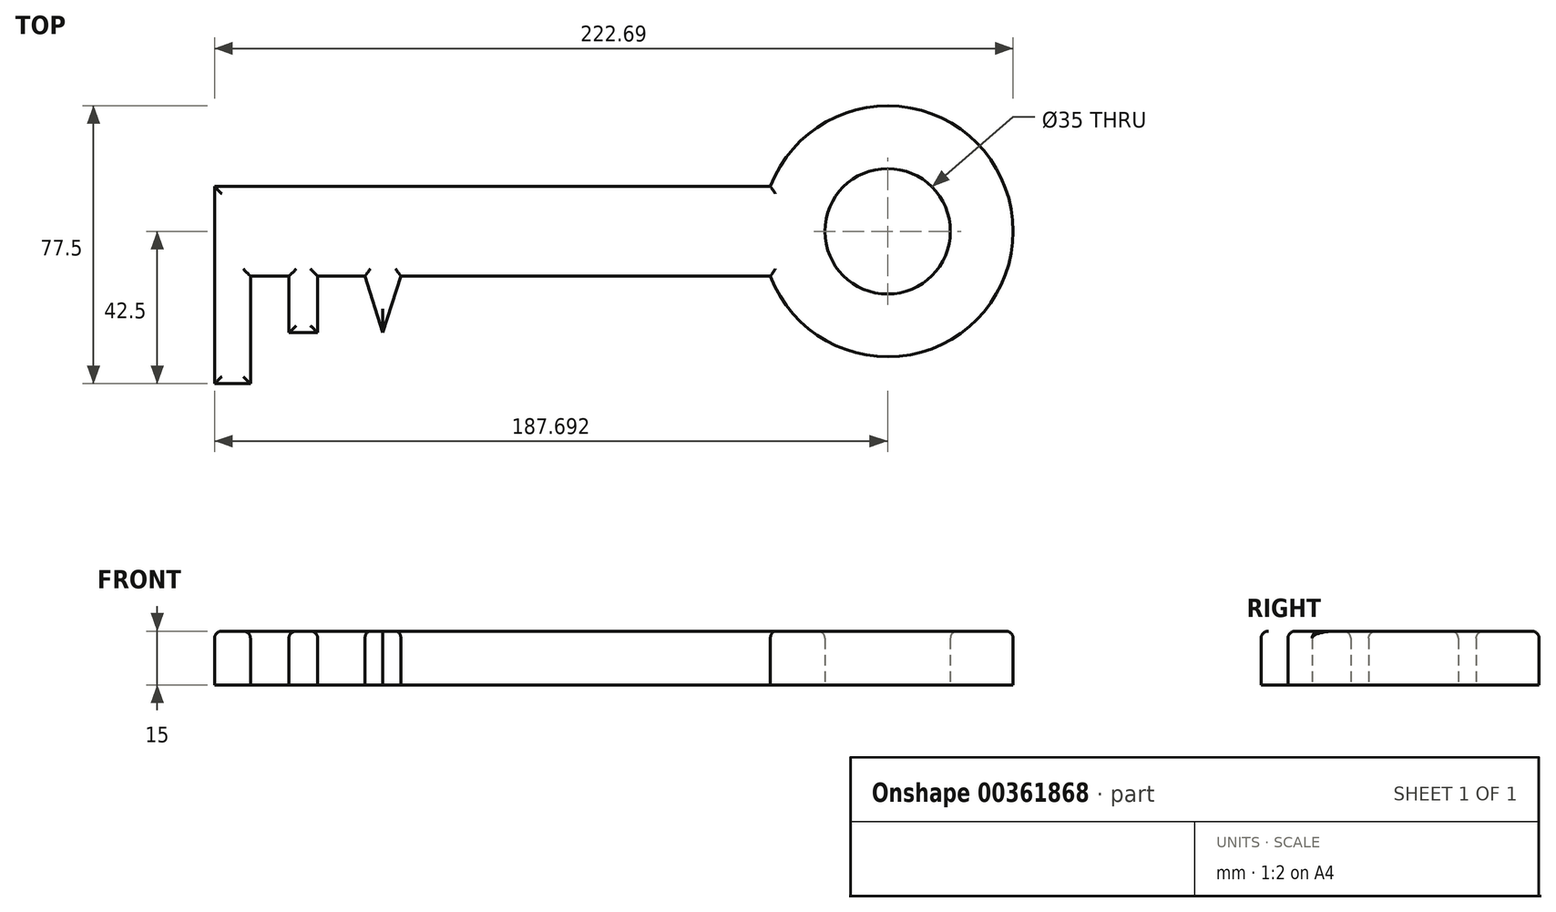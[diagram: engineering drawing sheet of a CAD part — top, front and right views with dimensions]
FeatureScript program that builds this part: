
annotation { "Feature Type Name" : "Feature", "Feature Type Description" : "" }
export const myFeature = defineFeature(function(context is Context, id is Id, definition is map)
    precondition{}
    {
        {
            var Q0;
            Q0=qCreatedBy(makeId("Top.planeOp"),FACE);
            var sketch = newSketch(context, id + "F0", { "sketchPlane" : qUnion([Q0])});
            skLineSegment(sketch, "E0.bottom", {"start": v(0, 15.78) * mm, "end": v(-155, 15.78) * mm});
            skLineSegment(sketch, "E0.top", {"start": v(0, 40.78) * mm, "end": v(-155, 40.78) * mm});
            skLineSegment(sketch, "E0.right", {"start": v(-155, 15.78) * mm, "end": v(-155, 40.78) * mm});
            skLineSegment(sketch, "E1.bottom", {"start": v(-155, 15.78) * mm, "end": v(-145, 15.78) * mm});
            skLineSegment(sketch, "E1.top", {"start": v(-155, -14.22) * mm, "end": v(-145, -14.22) * mm});
            skLineSegment(sketch, "E1.left", {"start": v(-155, 15.78) * mm, "end": v(-155, -14.22) * mm});
            skLineSegment(sketch, "E1.right", {"start": v(-145, 15.78) * mm, "end": v(-145, -14.22) * mm});
            skLineSegment(sketch, "E2.bottom", {"start": v(-134.26, 15.78) * mm, "end": v(-126.26, 15.78) * mm});
            skLineSegment(sketch, "E2.top", {"start": v(-134.26, 0) * mm, "end": v(-126.26, 0) * mm});
            skLineSegment(sketch, "E2.left", {"start": v(-134.26, 15.78) * mm, "end": v(-134.26, 0) * mm});
            skLineSegment(sketch, "E2.right", {"start": v(-126.26, 15.78) * mm, "end": v(-126.26, 0) * mm});
            skLineSegment(sketch, "E3", {"start": v(-113.05, 15.78) * mm, "end": v(-103.05, 15.78) * mm});
            skLineSegment(sketch, "E4", {"start": v(-113.05, 15.78) * mm, "end": v(-108.05, 0) * mm});
            skLineSegment(sketch, "E5", {"start": v(-108.05, 0) * mm, "end": v(-103.05, 15.78) * mm});
            skArc(sketch, "E6", {"start": v(0, 15.78) * mm, "mid": v(67.7, 28.28) * mm, "end": v(0, 40.78) * mm});
            skCircle(sketch, "E7", {"center": v(32.7, 28.28) * mm, "radius": 17.5 * mm});
            skSolve(sketch);
        }
        {
            var Q0;
            Q0 = qSketchRegion(id + "F0", true);
            extrude(context, id + "F1", {"entities" : qUnion([Q0]), "depth" : 15 * mm});
        }
        {
            var Q0;
            Q0=makeQuery(id+"F1.opExtrude","CAP_FACE",FACE,{"disambiguationData":[OSD([sQuery(id+"F0.wireOp",EDGE,"E0.bottom"),sQuery(id+"F0.wireOp",EDGE,"E0.top"),sQuery(id+"F0.wireOp",EDGE,"E0.right"),sQuery(id+"F0.wireOp",EDGE,"E1.top"),sQuery(id+"F0.wireOp",EDGE,"E1.left"),sQuery(id+"F0.wireOp",EDGE,"E1.right"),sQuery(id+"F0.wireOp",EDGE,"E2.top"),sQuery(id+"F0.wireOp",EDGE,"E2.left"),sQuery(id+"F0.wireOp",EDGE,"E2.right"),sQuery(id+"F0.wireOp",EDGE,"E4"),sQuery(id+"F0.wireOp",EDGE,"E5"),sQuery(id+"F0.wireOp",EDGE,"E6"),sQuery(id+"F0.wireOp",EDGE,"E7")])],"isStart":false});
            fillet(context, id + "F2", {"entities" : qUnion([Q0]), "radius" : 2 * mm, "tangentPropagation" : true, "allowEdgeOverflow" : false});
        }
    });
